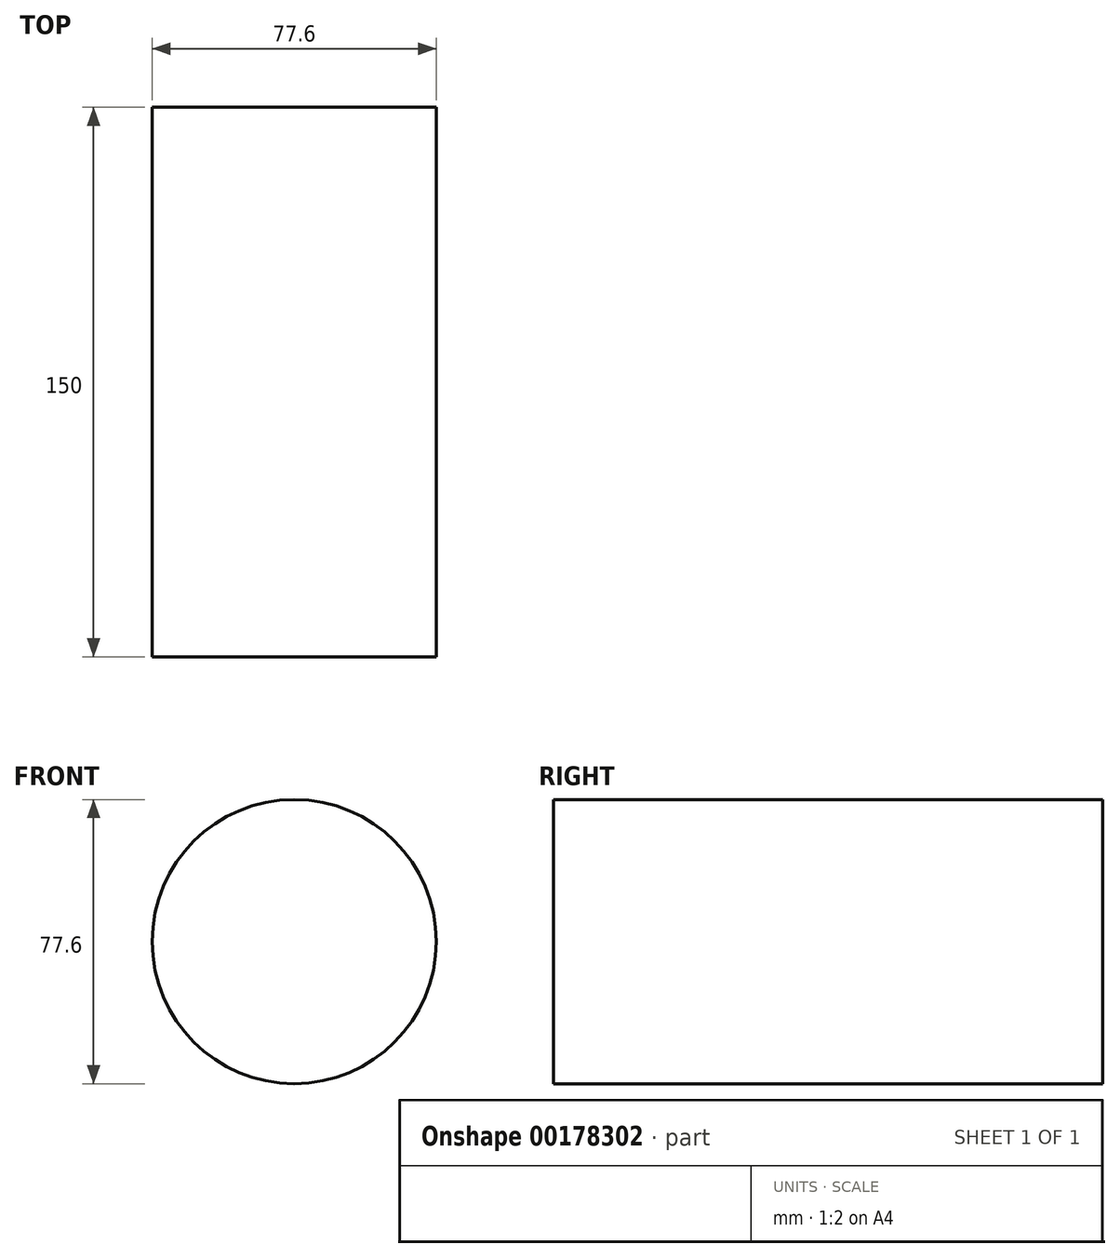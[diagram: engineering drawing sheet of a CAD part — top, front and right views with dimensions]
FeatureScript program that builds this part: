
annotation { "Feature Type Name" : "Feature", "Feature Type Description" : "" }
export const myFeature = defineFeature(function(context is Context, id is Id, definition is map)
    precondition{}
    {
        {
            var Q0;
            Q0=qCreatedBy(makeId("Front.planeOp"),FACE);
            var sketch = newSketch(context, id + "F0", { "sketchPlane" : qUnion([Q0])});
            skCircle(sketch, "E0", {"center": v(0, 0) * mm, "radius": 38.8 * mm});
            skSolve(sketch);
        }
        {
            var Q0;
            Q0 = qSketchRegion(id + "F0", true);
            extrude(context, id + "F1", {"entities" : qUnion([Q0]), "endBound" : BoundingType.SYMMETRIC, "depth" : 150 * mm});
        }
    });
